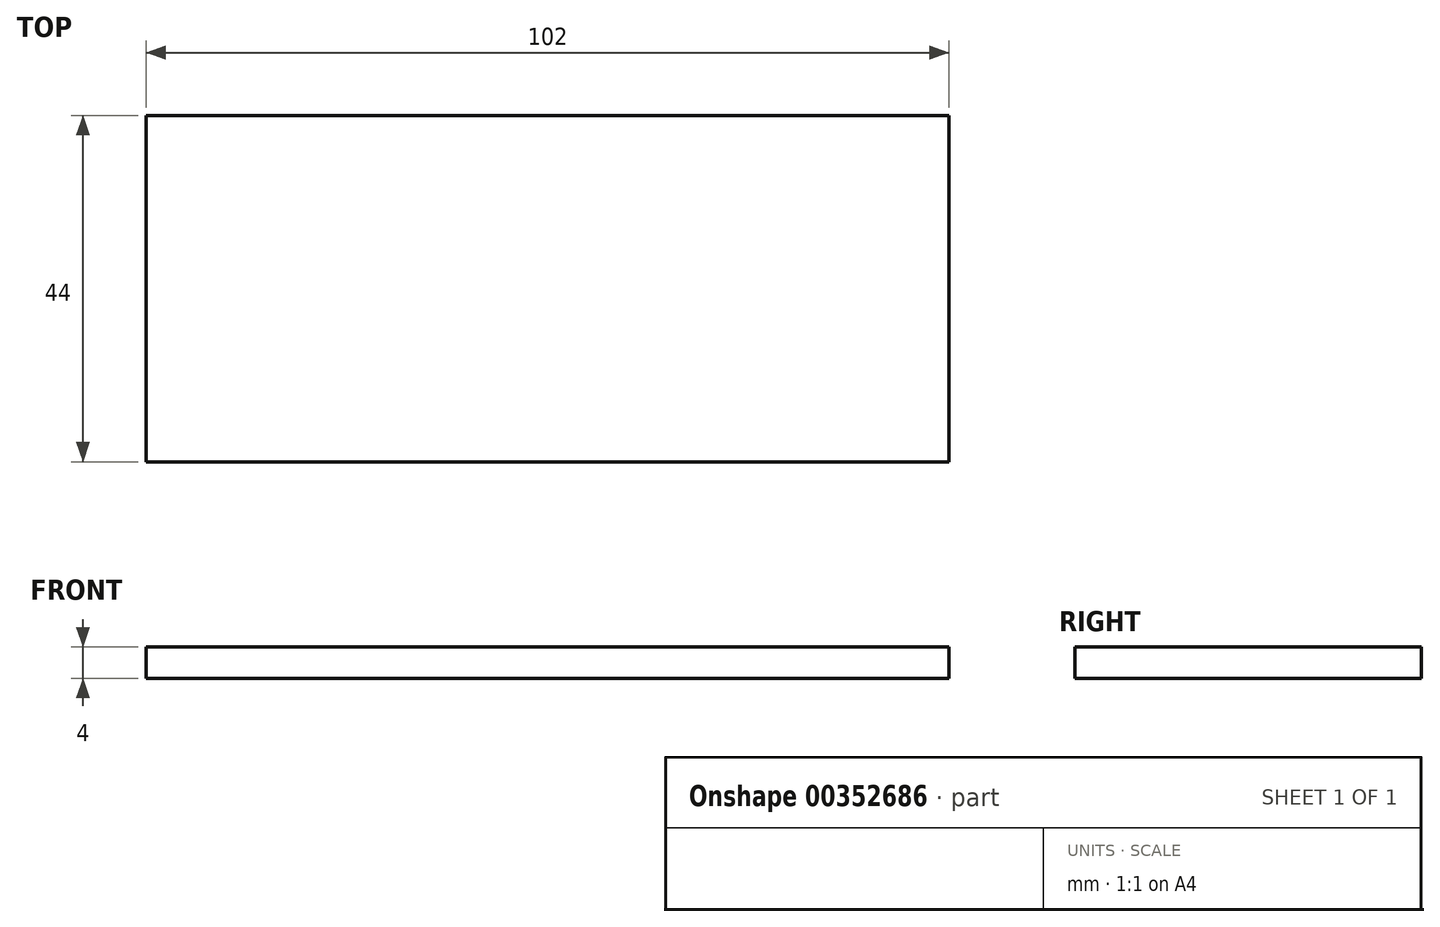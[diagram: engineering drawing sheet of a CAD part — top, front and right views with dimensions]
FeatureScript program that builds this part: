
annotation { "Feature Type Name" : "Feature", "Feature Type Description" : "" }
export const myFeature = defineFeature(function(context is Context, id is Id, definition is map)
    precondition{}
    {
        {
            var Q0;
            Q0=qCreatedBy(makeId("Top.planeOp"),FACE);
            var sketch = newSketch(context, id + "F0", { "sketchPlane" : qUnion([Q0])});
            skLineSegment(sketch, "E0.bottom", {"start": v(-51, 22) * mm, "end": v(51, 22) * mm});
            skLineSegment(sketch, "E0.top", {"start": v(-51, -22) * mm, "end": v(51, -22) * mm});
            skLineSegment(sketch, "E0.left", {"start": v(-51, 22) * mm, "end": v(-51, -22) * mm});
            skLineSegment(sketch, "E0.right", {"start": v(51, 22) * mm, "end": v(51, -22) * mm});
            skPoint(sketch, "E0.middle", {"position": v(0, 0) * mm});
            skSolve(sketch);
        }
        {
            var Q0;
            Q0=qSketchRegion(id+"F0",true);
            extrude(context, id + "F1", {"entities" : qUnion([Q0]), "depth" : 4 * mm});
        }
    });
